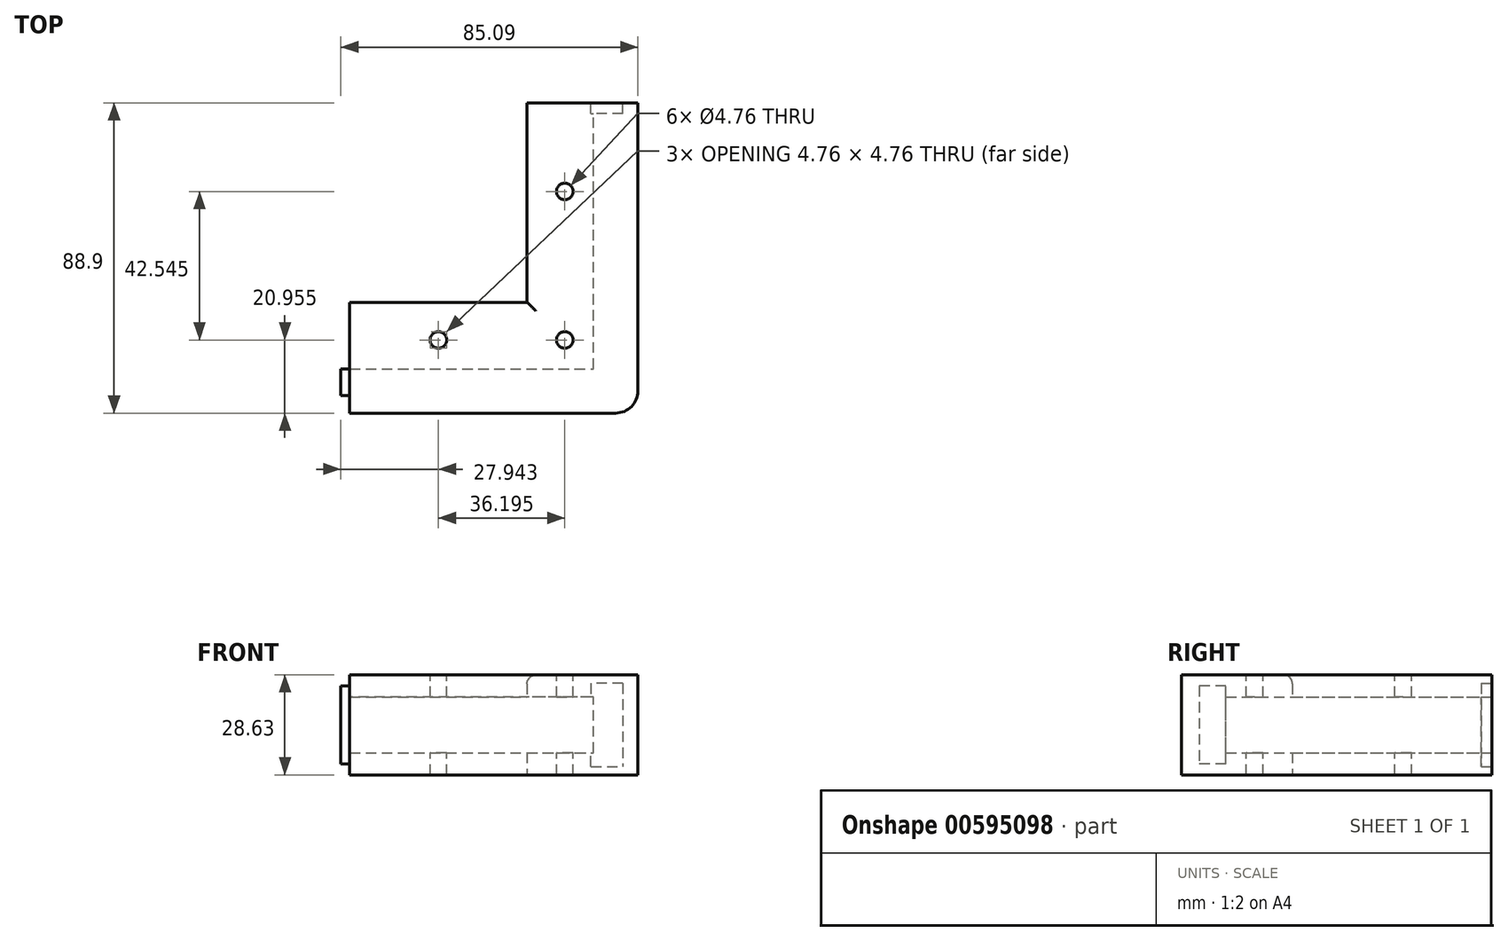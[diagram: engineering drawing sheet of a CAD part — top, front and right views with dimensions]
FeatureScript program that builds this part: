
annotation { "Feature Type Name" : "Feature", "Feature Type Description" : "" }
export const myFeature = defineFeature(function(context is Context, id is Id, definition is map)
    precondition{}
    {
        {
            var Q0;
            Q0=qCreatedBy(makeId("Front.planeOp"),FACE);
            var sketch = newSketch(context, id + "F0", { "sketchPlane" : qUnion([Q0])});
            skLineSegment(sketch, "E0", {"start": v(22.21, 16.91) * mm, "end": v(22.21, -11.72) * mm});
            skLineSegment(sketch, "E1", {"start": v(22.21, -11.72) * mm, "end": v(-9.54, -11.72) * mm});
            skLineSegment(sketch, "E2", {"start": v(-9.54, -11.72) * mm, "end": v(-9.54, -5.37) * mm});
            skLineSegment(sketch, "E3", {"start": v(-9.54, -5.37) * mm, "end": v(9.51, -5.37) * mm});
            skLineSegment(sketch, "E4", {"start": v(9.51, -5.37) * mm, "end": v(9.51, 10.56) * mm});
            skLineSegment(sketch, "E5", {"start": v(9.51, 10.56) * mm, "end": v(-9.54, 10.56) * mm});
            skLineSegment(sketch, "E6", {"start": v(22.21, 16.91) * mm, "end": v(-9.54, 16.91) * mm});
            skLineSegment(sketch, "E7", {"start": v(-9.54, 16.91) * mm, "end": v(-9.54, 10.56) * mm});
            skSolve(sketch);
        }
        {
            var Q0;
            Q0 = qSketchRegion(id + "F0", true);
            extrude(context, id + "F1", {"entities" : qUnion([Q0]), "depth" : 76.2 * mm, "offsetDistance" : 25.4 * mm});
        }
        {
            var Q0;
            Q0=makeQuery(id+"F1.opExtrude","SWEPT_FACE",FACE,{"disambiguationData":[OSD([sQuery(id+"F0.wireOp",EDGE,"E0")])]});
            var sketch = newSketch(context, id + "F2", { "sketchPlane" : qUnion([Q0])});
            skLineSegment(sketch, "E8", {"start": v(-76.2, 16.91) * mm, "end": v(-88.9, 16.91) * mm});
            skLineSegment(sketch, "E9", {"start": v(-88.9, 16.91) * mm, "end": v(-88.9, -11.72) * mm});
            skLineSegment(sketch, "E10", {"start": v(-88.9, -11.72) * mm, "end": v(-76.2, -11.72) * mm});
            skLineSegment(sketch, "E11", {"start": v(-76.2, -11.72) * mm, "end": v(-76.2, 16.91) * mm});
            skSolve(sketch);
        }
        {
            var Q0;
            Q0 = qSketchRegion(id + "F2", true);
            extrude(context, id + "F3", {"entities" : qUnion([Q0]), "operationType" : NewBodyOperationType.ADD, "oppositeDirection" : true, "depth" : 31.75 * mm, "offsetDistance" : 25.4 * mm});
        }
        {
            var Q0;
            Q0=makeQuery(id+"F3.boolean.opBoolean","MERGE",FACE,{"derivedFrom":[makeQuery(id+"F1.opExtrude","SWEPT_FACE",FACE,{"disambiguationData":[OSD([sQuery(id+"F0.wireOp",EDGE,"E2")])]}),makeQuery(id+"F1.opExtrude","SWEPT_FACE",FACE,{"disambiguationData":[OSD([sQuery(id+"F0.wireOp",EDGE,"E7")])]}),makeQuery(id+"F3.opExtrude","CAP_FACE",FACE,{"disambiguationData":[OSD([sQuery(id+"F2.wireOp",EDGE,"E8"),sQuery(id+"F2.wireOp",EDGE,"E9"),sQuery(id+"F2.wireOp",EDGE,"E10"),sQuery(id+"F2.wireOp",EDGE,"E11")])],"isStart":false})]});
            var sketch = newSketch(context, id + "F4", { "sketchPlane" : qUnion([Q0])});
            skLineSegment(sketch, "E12", {"start": v(88.9, 16.91) * mm, "end": v(57.15, 16.91) * mm});
            skLineSegment(sketch, "E13", {"start": v(57.15, 16.91) * mm, "end": v(57.15, 10.56) * mm});
            skLineSegment(sketch, "E14", {"start": v(57.15, 10.56) * mm, "end": v(76.2, 10.56) * mm});
            skLineSegment(sketch, "E15", {"start": v(76.2, 10.56) * mm, "end": v(76.2, -5.37) * mm});
            skLineSegment(sketch, "E16", {"start": v(76.2, -5.37) * mm, "end": v(57.15, -5.37) * mm});
            skLineSegment(sketch, "E17", {"start": v(57.15, -5.37) * mm, "end": v(57.15, -11.72) * mm});
            skLineSegment(sketch, "E18", {"start": v(88.9, -11.72) * mm, "end": v(88.9, 16.91) * mm});
            skLineSegment(sketch, "E19", {"start": v(57.15, -11.72) * mm, "end": v(88.9, -11.72) * mm});
            skSolve(sketch);
        }
        {
            var Q0;
            Q0 = qSketchRegion(id + "F4", true);
            extrude(context, id + "F5", {"entities" : qUnion([Q0]), "operationType" : NewBodyOperationType.ADD, "depth" : 50.8 * mm, "offsetDistance" : 25.4 * mm});
        }
        {
            var Q0;
            Q0=makeQuery(id+"F3.boolean.opBoolean","MERGE",EDGE,{"derivedFrom":[makeQuery(id+"F1.opExtrude","SWEPT_EDGE",EDGE,{"disambiguationData":[OSD([sQuery(id+"F0.wireOp",EDGE,"E6"),sQuery(id+"F0.wireOp",EDGE,"E7")])]}),makeQuery(id+"F3.opExtrude","CAP_EDGE",EDGE,{"disambiguationData":[OSD([sQuery(id+"F2.wireOp",EDGE,"E8")])],"isStart":false})]});
            fillet(context, id + "F6", {"entities" : qUnion([Q0]), "radius" : 2.54 * mm, "tangentPropagation" : true, "allowEdgeOverflow" : false});
        }
        {
            var Q0;
            Q0=makeQuery(id+"F5.opExtrude","SWEPT_EDGE",EDGE,{"disambiguationData":[OSD([sQuery(id+"F0.wireOp",EDGE,"E6"),sQuery(id+"F0.wireOp",EDGE,"E7"),sQuery(id+"F2.wireOp",EDGE,"E8"),sQuery(id+"F4.wireOp",EDGE,"E12"),sQuery(id+"F4.wireOp",EDGE,"E13")])]});
            fillet(context, id + "F7", {"entities" : qUnion([Q0]), "radius" : 2.54 * mm, "tangentPropagation" : true, "allowEdgeOverflow" : false});
        }
        {
            var Q0;
            Q0=makeQuery(id+"F3.opExtrude","CAP_EDGE",EDGE,{"disambiguationData":[OSD([sQuery(id+"F2.wireOp",EDGE,"E9")])],"isStart":true});
            fillet(context, id + "F8", {"entities" : qUnion([Q0]), "radius" : 6.35 * mm, "tangentPropagation" : true, "allowEdgeOverflow" : false});
        }
        {
            var Q0;
            Q0=makeQuery(id+"F5.boolean.opBoolean","MERGE",FACE,{"derivedFrom":[makeQuery(id+"F3.boolean.opBoolean","MERGE",FACE,{"derivedFrom":[makeQuery(id+"F1.opExtrude","SWEPT_FACE",FACE,{"disambiguationData":[OSD([sQuery(id+"F0.wireOp",EDGE,"E6")])]}),makeQuery(id+"F3.opExtrude","SWEPT_FACE",FACE,{"disambiguationData":[OSD([sQuery(id+"F2.wireOp",EDGE,"E8")])]})]}),makeQuery(id+"F5.opExtrude","SWEPT_FACE",FACE,{"disambiguationData":[OSD([sQuery(id+"F4.wireOp",EDGE,"E12")])]})]});
            var sketch = newSketch(context, id + "F9", { "sketchPlane" : qUnion([Q0])});
            skCircle(sketch, "E20", {"center": v(1.26, -67.95) * mm, "radius": 2.38 * mm});
            skCircle(sketch, "E21", {"center": v(1.26, -25.4) * mm, "radius": 2.38 * mm});
            skCircle(sketch, "E22", {"center": v(-34.94, -67.95) * mm, "radius": 2.38 * mm});
            skSolve(sketch);
        }
        {
            var Q0;
            Q0 = qSketchRegion(id + "F9", true);
            extrude(context, id + "F10", {"entities" : qUnion([Q0]), "operationType" : NewBodyOperationType.REMOVE, "oppositeDirection" : true, "depth" : 50.8 * mm, "offsetDistance" : 25.4 * mm});
        }
        {
            var Q0;
            Q0=makeQuery(id+"F5.opExtrude","CAP_FACE",FACE,{"disambiguationData":[OSD([sQuery(id+"F4.wireOp",EDGE,"E12"),sQuery(id+"F4.wireOp",EDGE,"E13"),sQuery(id+"F4.wireOp",EDGE,"E14"),sQuery(id+"F4.wireOp",EDGE,"E15"),sQuery(id+"F4.wireOp",EDGE,"E16"),sQuery(id+"F4.wireOp",EDGE,"E17"),sQuery(id+"F4.wireOp",EDGE,"ykkBHvsx-Sn6a-K4By-cm3h-KrFOhNhz2KJQ"),sQuery(id+"F4.wireOp",EDGE,"E18")])],"isStart":false});
            var sketch = newSketch(context, id + "F11", { "sketchPlane" : qUnion([Q0])});
            skPoint(sketch, "E23.orphan", {"position": v(57.15, 12.47) * mm});
            skPoint(sketch, "E24.orphan", {"position": v(57.15, -8.55) * mm});
            skLineSegment(sketch, "E25", {"start": v(76.2, 10.56) * mm, "end": v(76.2, 13.74) * mm});
            skLineSegment(sketch, "E26", {"start": v(76.2, 13.74) * mm, "end": v(83.82, 13.74) * mm});
            skLineSegment(sketch, "E27", {"start": v(83.82, 13.74) * mm, "end": v(83.82, -8.55) * mm});
            skLineSegment(sketch, "E28", {"start": v(76.2, -5.37) * mm, "end": v(76.2, -8.55) * mm});
            skLineSegment(sketch, "E29", {"start": v(76.2, -8.55) * mm, "end": v(83.82, -8.55) * mm});
            skLineSegment(sketch, "E30", {"start": v(76.2, -5.37) * mm, "end": v(76.2, 10.56) * mm});
            skSolve(sketch);
        }
        {
            var Q0;
            Q0 = qSketchRegion(id + "F11", true);
            extrude(context, id + "F12", {"entities" : qUnion([Q0]), "operationType" : NewBodyOperationType.ADD, "depth" : 2.54 * mm, "offsetDistance" : 25.4 * mm});
        }
        {
            var Q0;
            Q0=makeQuery(id+"F1.opExtrude","CAP_FACE",FACE,{"disambiguationData":[OSD([sQuery(id+"F0.wireOp",EDGE,"E0"),sQuery(id+"F0.wireOp",EDGE,"E1"),sQuery(id+"F0.wireOp",EDGE,"E2"),sQuery(id+"F0.wireOp",EDGE,"E3"),sQuery(id+"F0.wireOp",EDGE,"E4"),sQuery(id+"F0.wireOp",EDGE,"E5"),sQuery(id+"F0.wireOp",EDGE,"E6"),sQuery(id+"F0.wireOp",EDGE,"E7")])],"isStart":true});
            var sketch = newSketch(context, id + "F13", { "sketchPlane" : qUnion([Q0])});
            skLineSegment(sketch, "E31.bottom", {"start": v(-9.51, 14.5) * mm, "end": v(-17.9, 14.5) * mm});
            skLineSegment(sketch, "E31.top", {"start": v(-9.51, -9.31) * mm, "end": v(-17.9, -9.31) * mm});
            skLineSegment(sketch, "E31.left", {"start": v(-9.51, 10.56) * mm, "end": v(-9.51, -5.37) * mm});
            skLineSegment(sketch, "E31.right", {"start": v(-17.9, 14.5) * mm, "end": v(-17.9, -9.31) * mm});
            skLineSegment(sketch, "E32.bottom", {"start": v(-9.51, 14.5) * mm, "end": v(-8.75, 14.5) * mm});
            skLineSegment(sketch, "E32.top", {"start": v(-9.51, 10.56) * mm, "end": v(-8.75, 10.56) * mm});
            skLineSegment(sketch, "E32.right", {"start": v(-8.75, 14.5) * mm, "end": v(-8.75, 10.56) * mm});
            skLineSegment(sketch, "E33.bottom", {"start": v(-9.51, -9.31) * mm, "end": v(-8.75, -9.31) * mm});
            skLineSegment(sketch, "E33.top", {"start": v(-9.51, -5.37) * mm, "end": v(-8.75, -5.37) * mm});
            skLineSegment(sketch, "E33.right", {"start": v(-8.75, -9.31) * mm, "end": v(-8.75, -5.37) * mm});
            skLineSegment(sketch, "E34", {"start": v(-8.75, 10.56) * mm, "end": v(-9.51, 10.56) * mm});
            skLineSegment(sketch, "E35", {"start": v(-8.75, -5.37) * mm, "end": v(-9.51, -5.37) * mm});
            skSolve(sketch);
        }
        {
            var Q0;
            Q0 = qSketchRegion(id + "F13", true);
            extrude(context, id + "F14", {"entities" : qUnion([Q0]), "operationType" : NewBodyOperationType.REMOVE, "oppositeDirection" : true, "depth" : 3.05 * mm, "offsetDistance" : 25.4 * mm});
        }
    });
